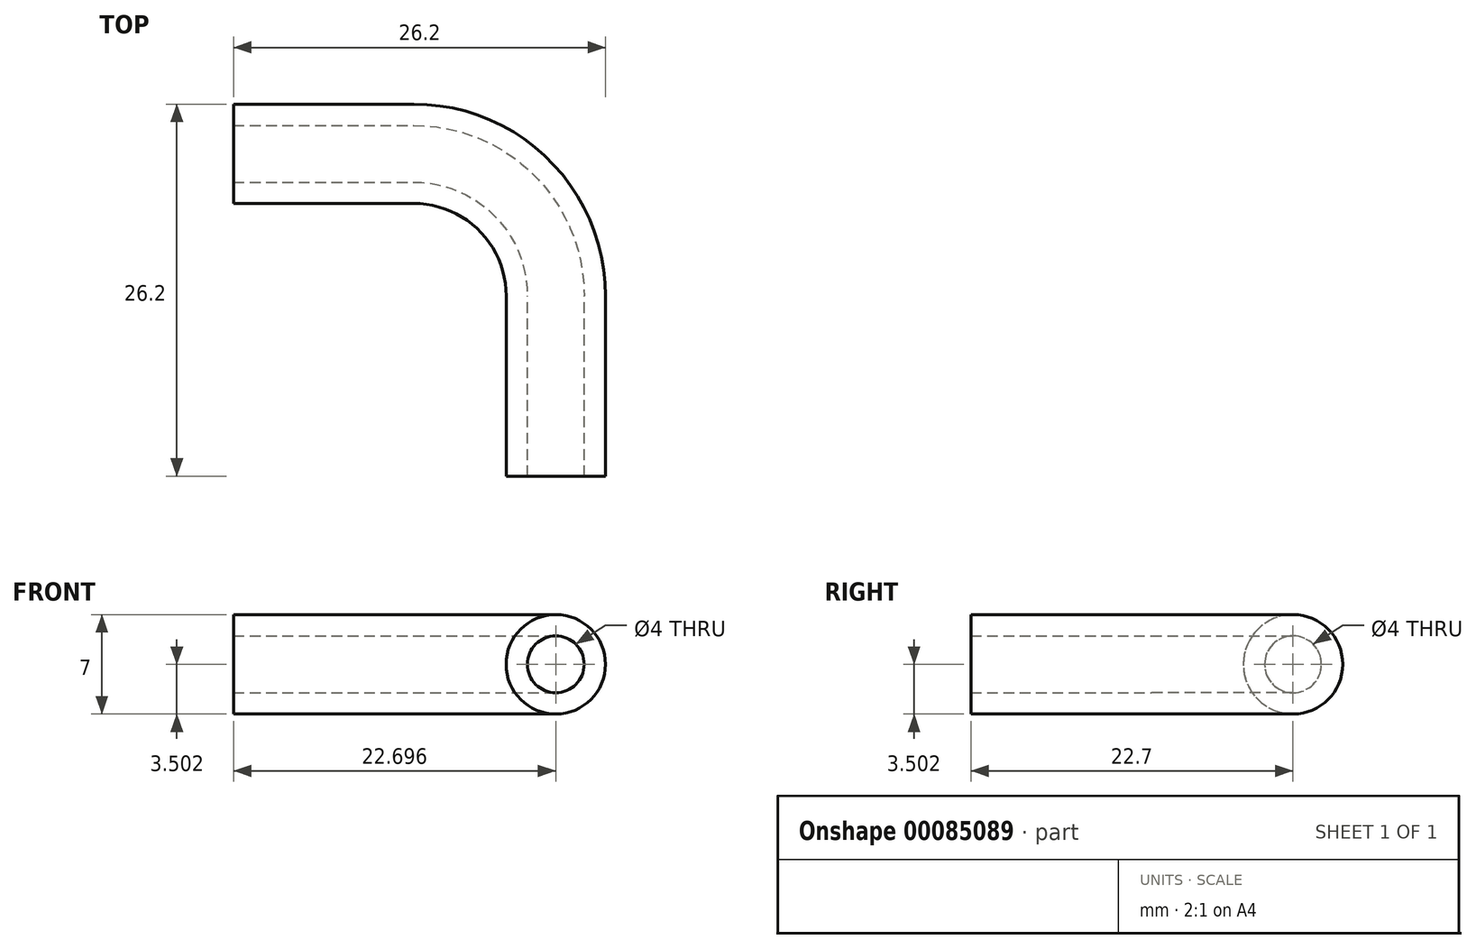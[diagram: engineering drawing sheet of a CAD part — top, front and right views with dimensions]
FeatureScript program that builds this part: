
annotation { "Feature Type Name" : "Feature", "Feature Type Description" : "" }
export const myFeature = defineFeature(function(context is Context, id is Id, definition is map)
    precondition{}
    {
        {
            var Q0;
            Q0=qCreatedBy(makeId("Front.planeOp"),FACE);
            var sketch = newSketch(context, id + "F0", { "sketchPlane" : qUnion([Q0])});
            skCircle(sketch, "E0", {"center": v(-3.47, 10.08) * mm, "radius": 3.5 * mm});
            skCircle(sketch, "E1", {"center": v(-3.47, 10.08) * mm, "radius": 2 * mm});
            skSolve(sketch);
        }
        {
            var Q0;
            Q0=qSketchRegion(id+"F0",true);
            extrude(context, id + "F1", {"entities" : qUnion([Q0]), "depth" : 12.7 * mm});
        }
        {
            var Q0;
            Q0=makeQuery(id+"F1.opExtrude","CAP_FACE",FACE,{"disambiguationData":[OSD([sQuery(id+"F0.wireOp",EDGE,"E0"),sQuery(id+"F0.wireOp",EDGE,"E1")])],"isStart":true});
            var sketch = newSketch(context, id + "F2", { "sketchPlane" : qUnion([Q0])});
            skLineSegment(sketch, "E2", {"start": v(13.47, 13.73) * mm, "end": v(13.47, 6.04) * mm});
            skCircle(sketch, "E3.0.0", {"center": v(3.47, 10.08) * mm, "radius": 3.5 * mm});
            skCircle(sketch, "E4.0", {"center": v(3.47, 10.08) * mm, "radius": 2 * mm});
            skSolve(sketch);
        }
        {
            var Q0;
            Q0 = qSketchRegion(id + "F2", true);
            var Q1;
            Q1=sQuery(id+"F2.wireOp",EDGE,"E2");
            revolve(context, id + "F3", {"operationType" : NewBodyOperationType.ADD, "entities" : qUnion([Q0]), "axis" : qUnion([Q1]), "revolveType" : RevolveType.ONE_DIRECTION, "oppositeDirection" : true, "angle" : 90 * degree});
        }
        {
            var Q0;
            Q0=makeQuery(id+"F3.opRevolve","CAP_FACE",FACE,{"disambiguationData":[OSD([sQuery(id+"F2.wireOp",EDGE,"E3.0.0"),sQuery(id+"F2.wireOp",EDGE,"E4.0")])],"isStart":false});
            var sketch = newSketch(context, id + "F4", { "sketchPlane" : qUnion([Q0])});
            skCircle(sketch, "E5.0.0", {"center": v(-10, 10.08) * mm, "radius": 3.5 * mm});
            skSolve(sketch);
        }
        {
            var Q0;
            Q0=makeQuery(id+"F4.imprint","IMPRINT",FACE,{"disambiguationData":[TD([[makeQuery(id+"F4.imprint","IMPRINT",EDGE,{"derivedFrom":sQuery(id+"F4.wireOp",EDGE,"E5.0.0")}),-1.0]])]});
            extrude(context, id + "F5", {"entities" : qUnion([Q0]), "operationType" : NewBodyOperationType.ADD, "depth" : 12.7 * mm});
        }
    });
